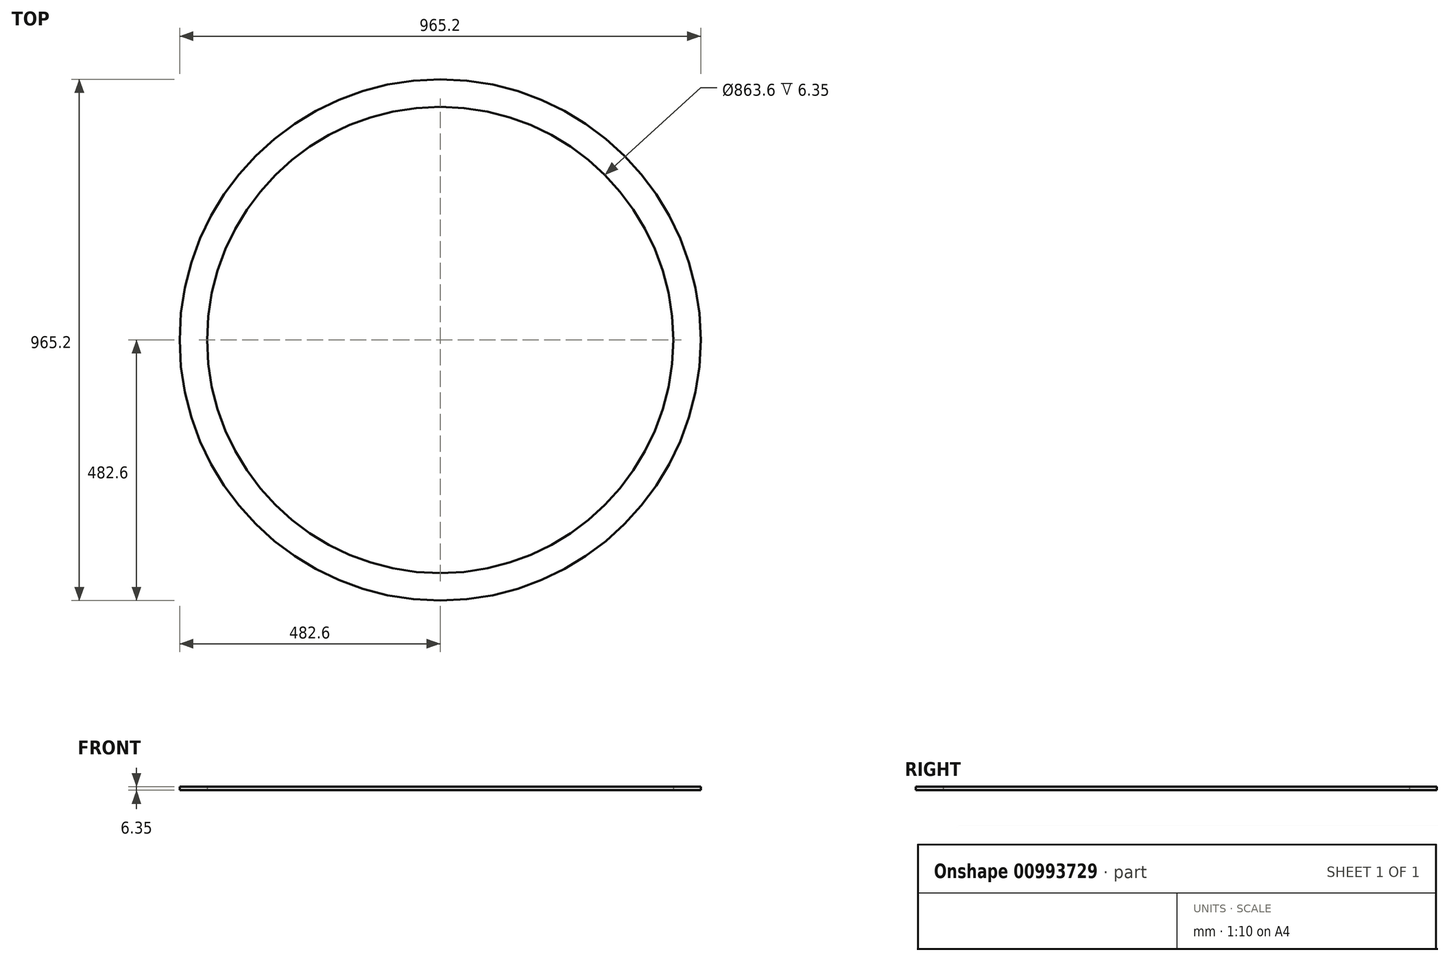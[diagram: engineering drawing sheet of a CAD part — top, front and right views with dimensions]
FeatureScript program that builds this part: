
annotation { "Feature Type Name" : "Feature", "Feature Type Description" : "" }
export const myFeature = defineFeature(function(context is Context, id is Id, definition is map)
    precondition{}
    {
        {
            var Q0;
            Q0=qCreatedBy(makeId("Top.planeOp"),FACE);
            var sketch = newSketch(context, id + "F0", { "sketchPlane" : qUnion([Q0])});
            skCircle(sketch, "E0", {"center": v(0, 0) * mm, "radius": 482.6 * mm});
            skCircle(sketch, "E1", {"center": v(0, 0) * mm, "radius": 431.8 * mm});
            skSolve(sketch);
        }
        {
            var Q0;
            Q0=makeQuery(id+"F0.imprint","IMPRINT",FACE,{"disambiguationData":[TD([[makeQuery(id+"F0.imprint","IMPRINT",EDGE,{"derivedFrom":sQuery(id+"F0.wireOp",EDGE,"E0")}),1.0]])]});
            extrude(context, id + "F1", {"entities" : qUnion([Q0]), "depth" : 6.35 * mm, "offsetDistance" : 25.4 * mm});
        }
    });
